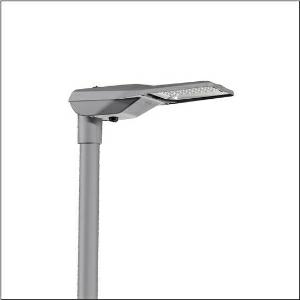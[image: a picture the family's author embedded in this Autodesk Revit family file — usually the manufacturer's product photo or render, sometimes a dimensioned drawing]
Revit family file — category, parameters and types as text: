
# Revit family: streetlight_sl_21_iq_mini___st1_5a_5xe2p31y08hb_ad09
name_source: partatom
category: Lighting Fixtures
units: mm (PartAtom-declared; Revit-internal decimal feet)

## family parameters
Cut with Voids When Loaded = No
Host = Face
Light Source = No
Part Type = Normal
Room Calculation Point = No
Round Connector Dimension = Use Diameter
Shared = No

## types (1)
- --- (1 x LED, 9580 lm, 71 W, 3000K)
    Apparent Load = 71 VA
    CIE Flux Codes = 22 53 95 100 100
    Color Rendering = 70
    Color Temperature = 3000K
    Default Elevation = 1800 mm
    Description = Streetlight SL 21 iQ mini, mast luminaire, primary light control with lens, of PMMA, primary optical cover: cover, of toughened safety glass, transparent, light distribution: ST1.5a, light emission: direct distribution, primary light characteristic: asymmetric, installation type: post-top, side-entry, LED, High Power LED, rated luminous flux: 9.580lm, luminous efficacy: 135lm/W, light colour: 730, colour temperature: 3000K, control gear: iQ-Street Remote, D4i with power reduction, control: pre-setting: logarithmic dimming characteristic, Street-Remote, Auto-Match, Temp-Guard, Lumen-Switch, Night-Set, Smart-Wire, Light-Fading, Desk-Remote (wireless, voltage-free reading and setting of iQ features in the workshop via application-optimized NFC function/RFID function), optimised constant luminous flux control (CLO 2.0), mains connection: 220..240V, AC, 50/60Hz, start of lifetime: 71W, end of service life: 75W, reduction: 30W, luminaire housing, of diecast aluminium, powder-coated, SITECO metallic grey (DB 702S), corrosivity category C5 high according to DIN EN ISO 12944, please order mast flange separately, inclination adjustable: 0°, 5°, 10°, 15°, sealing non-destructively replaceable, multi-level sealing system, length: 628mm, width: 235mm, height: 110mm, mast flange for spigot size: 42mm (side-entry): 5XC10008XM4, 60/48mm (side-entry/post-top): 5XC10108XM2, 76/60mm (side-entry/post-top): 5XC10108XM1, mounting height: 4..8m, Smart Interface below and above, protection rating (complete): IP66, insulation class (complete): insulation class II (safety insulation), certification: CE, ENEC, ENEC+, VDE, impact resistance: IK10, permissible operating ambient temperature for outdoor applications: -40..+50°C, standard-compliant lighting for roads and squares, packaging unit: 1 piece

Light Distribution: ST1.5a
    Height = 110 mm
    Lamp = 1 x LED
    Lamp Light Flux = 9580 lm
    Lamp Power = 71 W
    Lamp count = 1
    Length = 625 mm
    Luminous efficacy = 135 lm/W
    Manufacturer = Siteco
    ModVariant = No
    Model = 5XE2P31Y08HB
    Number of Poles = 1
    OnlyDefault = Yes
    Power Factor = 1
    Product Name = Streetlight SL 21 iQ mini | ST1.5a
    Product group = mast luminaire | pylon top
    ProductGroupID = 6100
    Protection Class = Protection class II
    Protection Degree = IP 66
    RLX_Detail_Level = 1
    RLX_Emergency_Light_Flux = 0 lm
    RLX_Emergency_Type = 0
    RLX_Emergency_Type_DB = No
    RlxData = <blob elided: 96701 chars, md5=6b2df393>
    Socket = socket
    Standby Power = 0 W
    System Light Flux = 9580 lm
    System Power = 71 W
    Type Comments = factory setting: luminous flux: 100 % | dim-lin: 254 | 716 mA
    Type Image = l_1003514.jpg
    URL = http://relux.com
    VarID = @adj_111851
    Voltage = 0 V
    Weight = 0.00 kg
    Width = 234 mm

## geometry (parser evidence)
native form markers: Blend x4, Sweep x12
no freeform markers — native parametric forms only
